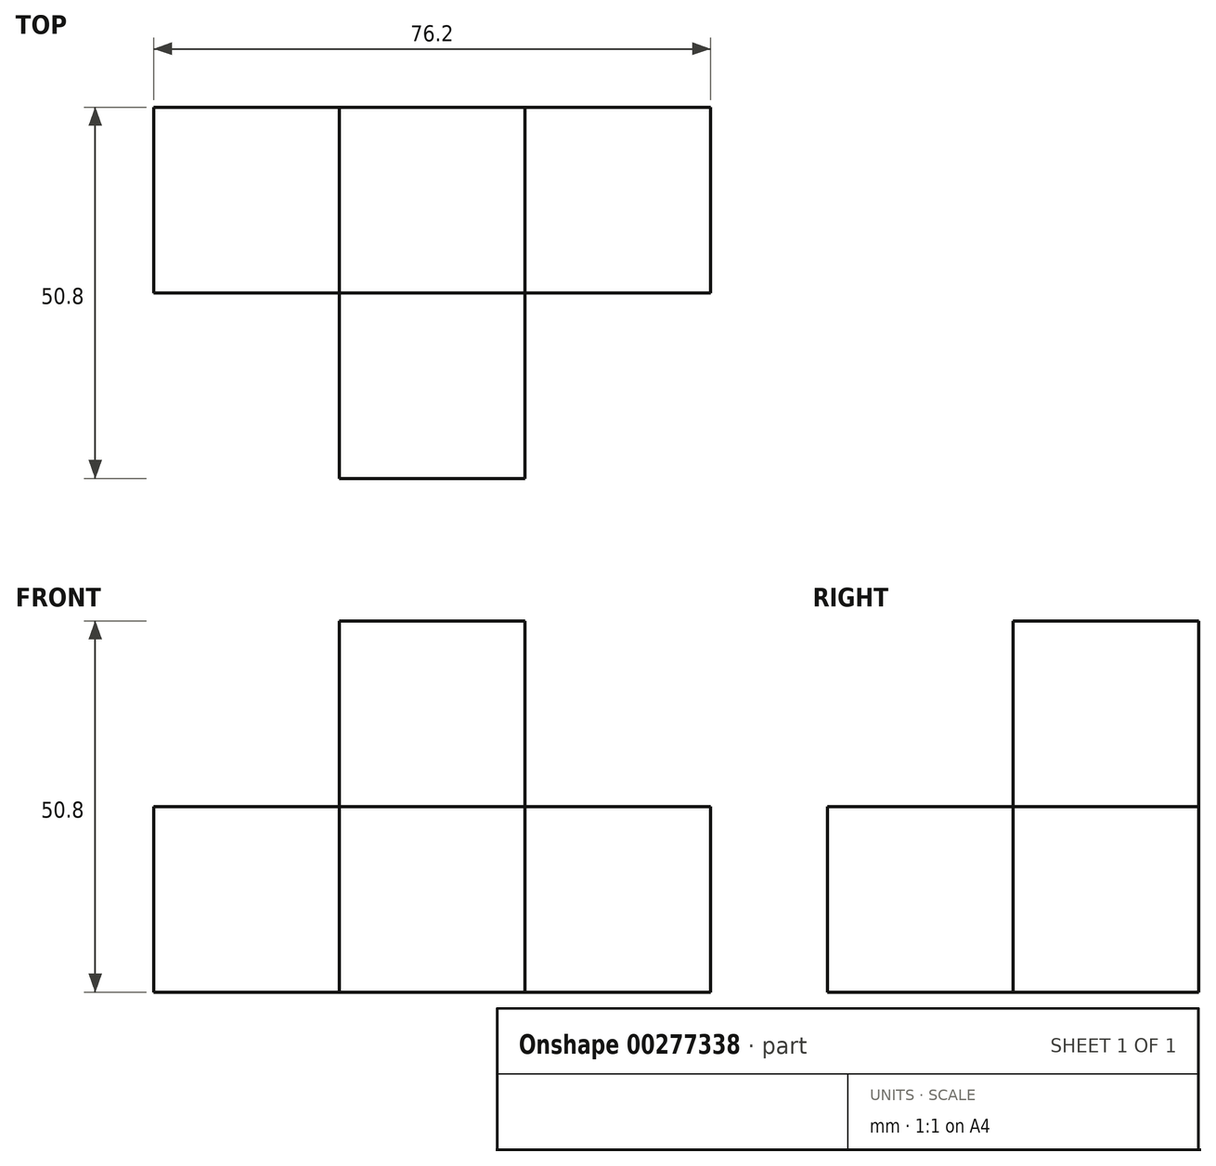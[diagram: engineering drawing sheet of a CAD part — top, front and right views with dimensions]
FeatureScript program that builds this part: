
annotation { "Feature Type Name" : "Feature", "Feature Type Description" : "" }
export const myFeature = defineFeature(function(context is Context, id is Id, definition is map)
    precondition{}
    {
        {
            var Q0;
            Q0=qCreatedBy(makeId("Front.planeOp"),FACE);
            var sketch = newSketch(context, id + "F0", { "sketchPlane" : qUnion([Q0])});
            skLineSegment(sketch, "E0", {"start": v(-40.88, -20.26) * mm, "end": v(-15.48, -20.26) * mm});
            skLineSegment(sketch, "E1", {"start": v(-15.48, -20.26) * mm, "end": v(9.92, -20.26) * mm});
            skLineSegment(sketch, "E2", {"start": v(9.92, -20.26) * mm, "end": v(35.32, -20.26) * mm});
            skLineSegment(sketch, "E3", {"start": v(35.32, -20.26) * mm, "end": v(35.32, 5.14) * mm});
            skLineSegment(sketch, "E4", {"start": v(35.32, 5.14) * mm, "end": v(9.92, 5.14) * mm});
            skLineSegment(sketch, "E5", {"start": v(9.92, 5.14) * mm, "end": v(-15.48, 5.14) * mm});
            skLineSegment(sketch, "E6", {"start": v(-15.48, 5.14) * mm, "end": v(-40.88, 5.14) * mm});
            skLineSegment(sketch, "E7", {"start": v(-40.88, 5.14) * mm, "end": v(-40.88, -20.26) * mm});
            skLineSegment(sketch, "E8", {"start": v(-15.48, 5.14) * mm, "end": v(-15.48, 30.54) * mm});
            skLineSegment(sketch, "E9", {"start": v(-15.48, 30.54) * mm, "end": v(9.92, 30.54) * mm});
            skLineSegment(sketch, "E10", {"start": v(9.92, 30.54) * mm, "end": v(9.92, 5.14) * mm});
            skLineSegment(sketch, "E11", {"start": v(9.92, 5.14) * mm, "end": v(9.92, -20.26) * mm});
            skLineSegment(sketch, "E12", {"start": v(-15.48, 5.14) * mm, "end": v(-15.48, -20.26) * mm});
            skSolve(sketch);
        }
        {
            var Q0;
            Q0=makeQuery(id+"F0.imprint","IMPRINT",FACE,{"disambiguationData":[TD([[makeQuery(id+"F0.imprint","IMPRINT",EDGE,{"derivedFrom":sQuery(id+"F0.wireOp",EDGE,"E1")}),1.0]])]});
            extrude(context, id + "F1", {"entities" : qUnion([Q0]), "depth" : 50.8 * mm});
        }
        {
            var Q0;
            Q0=makeQuery(id+"F0.imprint","IMPRINT",FACE,{"disambiguationData":[TD([[makeQuery(id+"F0.imprint","IMPRINT",EDGE,{"derivedFrom":sQuery(id+"F0.wireOp",EDGE,"E0")}),1.0]])]});
            var Q1;
            Q1=makeQuery(id+"F0.imprint","IMPRINT",FACE,{"disambiguationData":[TD([[makeQuery(id+"F0.imprint","IMPRINT",EDGE,{"derivedFrom":sQuery(id+"F0.wireOp",EDGE,"E5")}),-1.0]])]});
            var Q2;
            Q2=makeQuery(id+"F0.imprint","IMPRINT",FACE,{"disambiguationData":[TD([[makeQuery(id+"F0.imprint","IMPRINT",EDGE,{"derivedFrom":sQuery(id+"F0.wireOp",EDGE,"E2")}),1.0]])]});
            extrude(context, id + "F2", {"entities" : qUnion([Q0, Q1, Q2]), "operationType" : NewBodyOperationType.ADD, "depth" : 25.4 * mm});
        }
    });
